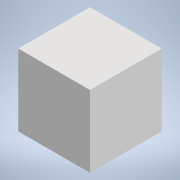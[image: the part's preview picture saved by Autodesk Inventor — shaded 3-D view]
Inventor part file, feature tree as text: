
AUTODESK INVENTOR PART (.ipt)
format: ipt  version: 2022 (Build 260153000, 153)  size: 86,528 bytes
history: native  units: mm
features: extrude x1, sketch x1
ambient origin geometry x8: Origin, YZ Plane, XZ Plane, XY Plane, X Axis, Y Axis, Z Axis, Center Point
bodies: Solid1 (feature_tree)
feature tree (2):
  extrude  "Extrusion1"  Depth=20.0mm
  sketch  "Sketch1"  dims[d0=20.0mm d1=20.0mm d2=10.0mm d3=10.0mm d4=20.0mm d5=0.0mm]
